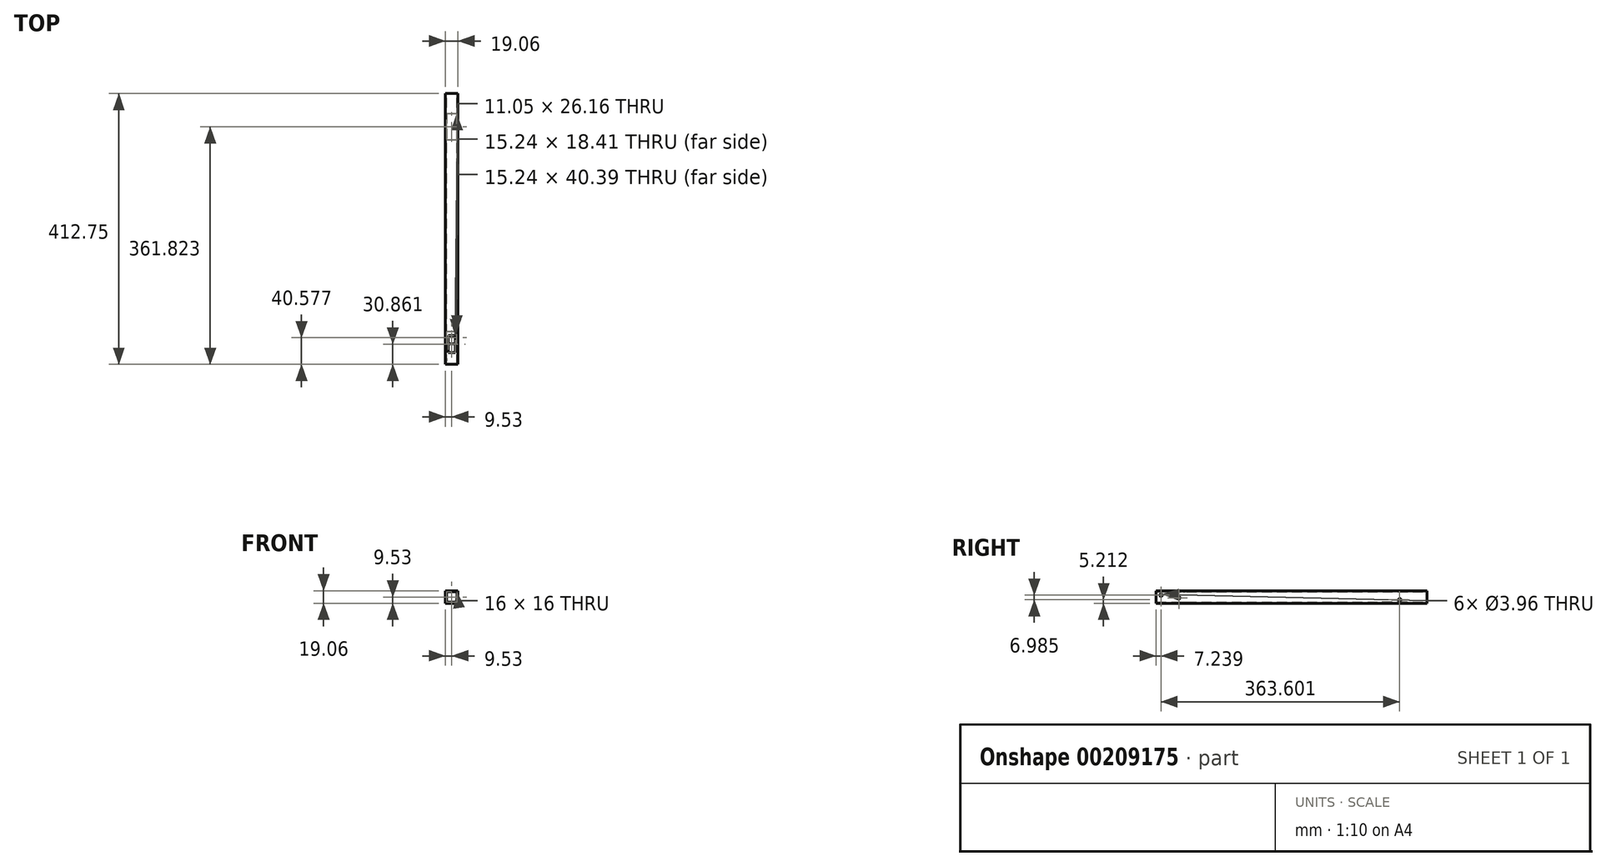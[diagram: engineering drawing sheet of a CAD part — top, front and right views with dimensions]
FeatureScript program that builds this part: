
annotation { "Feature Type Name" : "Feature", "Feature Type Description" : "" }
export const myFeature = defineFeature(function(context is Context, id is Id, definition is map)
    precondition{}
    {
        {
            var Q0;
            Q0=qCreatedBy(makeId("Front.planeOp"),FACE);
            var sketch = newSketch(context, id + "F0", { "sketchPlane" : qUnion([Q0])});
            skLineSegment(sketch, "E0.bottom", {"start": v(9.53, 9.53) * mm, "end": v(-9.53, 9.53) * mm});
            skLineSegment(sketch, "E0.top", {"start": v(9.53, -9.53) * mm, "end": v(-9.53, -9.53) * mm});
            skLineSegment(sketch, "E0.left", {"start": v(9.53, 9.53) * mm, "end": v(9.53, -9.53) * mm});
            skLineSegment(sketch, "E0.right", {"start": v(-9.53, 9.53) * mm, "end": v(-9.53, -9.53) * mm});
            skPoint(sketch, "E0.middle", {"position": v(0, 0) * mm});
            skLineSegment(sketch, "E1.0", {"start": v(8, 8) * mm, "end": v(-8, 8) * mm});
            skLineSegment(sketch, "E1.1", {"start": v(8, 8) * mm, "end": v(8, -8) * mm});
            skLineSegment(sketch, "E1.2", {"start": v(8, -8) * mm, "end": v(-8, -8) * mm});
            skLineSegment(sketch, "E1.3", {"start": v(-8, 8) * mm, "end": v(-8, -8) * mm});
            skSolve(sketch);
        }
        {
            var Q0;
            Q0 = qSketchRegion(id + "F0", true);
            extrude(context, id + "F1", {"entities" : qUnion([Q0]), "depth" : 412.75 * mm});
        }
        {
            var Q0;
            Q0=qCreatedBy(makeId("Right.planeOp"),FACE);
            var sketch = newSketch(context, id + "F2", { "sketchPlane" : qUnion([Q0])});
            skCircle(sketch, "E2", {"center": v(-405.51, 2.67) * mm, "radius": 1.98 * mm});
            skCircle(sketch, "E3", {"center": v(-378.33, -1.4) * mm, "radius": 1.98 * mm});
            skCircle(sketch, "E4", {"center": v(-41.91, -4.32) * mm, "radius": 1.98 * mm});
            skSolve(sketch);
        }
        {
            var Q0;
            Q0 = qSketchRegion(id + "F2", true);
            extrude(context, id + "F3", {"entities" : qUnion([Q0]), "operationType" : NewBodyOperationType.REMOVE, "oppositeDirection" : true, "depth" : 25.4 * mm, "hasSecondDirection" : true, "secondDirectionOppositeDirection" : false, "secondDirectionDepth" : 25.4 * mm});
        }
        {
            var Q0;
            Q0=makeQuery(id+"F1.opExtrude","SWEPT_FACE",FACE,{"disambiguationData":[OSD([sQuery(id+"F0.wireOp",EDGE,"E0.top")])]});
            var sketch = newSketch(context, id + "F4", { "sketchPlane" : qUnion([Q0])});
            skLineSegment(sketch, "E5.bottom", {"start": v(7.62, 30.73) * mm, "end": v(-7.62, 30.73) * mm});
            skLineSegment(sketch, "E5.top", {"start": v(7.62, 71.12) * mm, "end": v(-7.62, 71.12) * mm});
            skLineSegment(sketch, "E5.left", {"start": v(7.62, 30.73) * mm, "end": v(7.62, 71.12) * mm});
            skLineSegment(sketch, "E5.right", {"start": v(-7.62, 30.73) * mm, "end": v(-7.62, 71.12) * mm});
            skPoint(sketch, "E5.middle", {"position": v(0, 50.93) * mm});
            skLineSegment(sketch, "E6.bottom", {"start": v(7.62, 381.38) * mm, "end": v(-7.62, 381.38) * mm});
            skLineSegment(sketch, "E6.top", {"start": v(7.62, 362.97) * mm, "end": v(-7.62, 362.97) * mm});
            skLineSegment(sketch, "E6.left", {"start": v(7.62, 381.38) * mm, "end": v(7.62, 362.97) * mm});
            skLineSegment(sketch, "E6.right", {"start": v(-7.62, 381.38) * mm, "end": v(-7.62, 362.97) * mm});
            skPoint(sketch, "E6.middle", {"position": v(0, 372.17) * mm});
            skSolve(sketch);
        }
        {
            var Q0;
            Q0 = qSketchRegion(id + "F4", true);
            extrude(context, id + "F5", {"entities" : qUnion([Q0]), "operationType" : NewBodyOperationType.REMOVE, "oppositeDirection" : true, "depth" : 6.35 * mm});
        }
        {
            var Q0;
            Q0=makeQuery(id+"F1.opExtrude","SWEPT_FACE",FACE,{"disambiguationData":[OSD([sQuery(id+"F0.wireOp",EDGE,"E0.bottom")])]});
            var sketch = newSketch(context, id + "F6", { "sketchPlane" : qUnion([Q0])});
            skLineSegment(sketch, "E7.bottom", {"start": v(5.52, -368.8) * mm, "end": v(-5.52, -368.8) * mm});
            skLineSegment(sketch, "E7.top", {"start": v(5.52, -394.97) * mm, "end": v(-5.52, -394.97) * mm});
            skLineSegment(sketch, "E7.left", {"start": v(5.52, -368.8) * mm, "end": v(5.52, -394.97) * mm});
            skLineSegment(sketch, "E7.right", {"start": v(-5.52, -368.8) * mm, "end": v(-5.52, -394.97) * mm});
            skPoint(sketch, "E7.middle", {"position": v(0, -381.89) * mm});
            skSolve(sketch);
        }
        {
            var Q0;
            Q0 = qSketchRegion(id + "F6", true);
            extrude(context, id + "F7", {"entities" : qUnion([Q0]), "operationType" : NewBodyOperationType.REMOVE, "oppositeDirection" : true, "depth" : 6.35 * mm});
        }
    });
